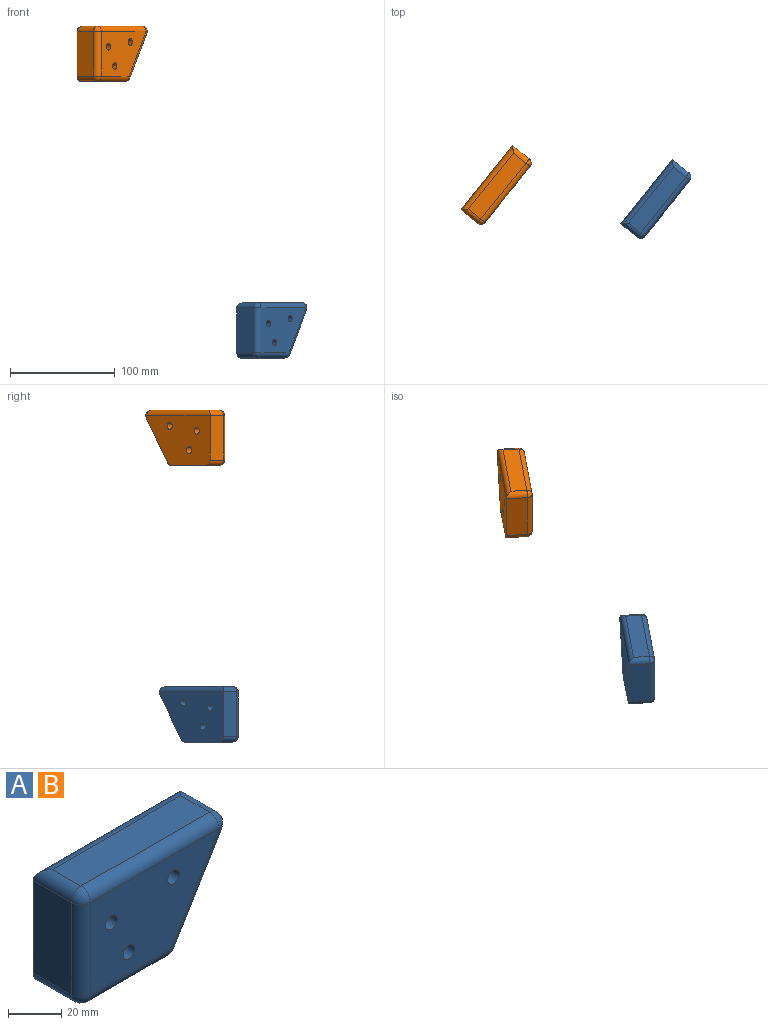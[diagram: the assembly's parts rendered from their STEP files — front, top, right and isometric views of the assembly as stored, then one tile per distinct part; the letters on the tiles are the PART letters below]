
ASSEMBLY  parts=2 mates=1
PART A: 22 faces, bbox 78.6x25.4x52.9 mm
  f0: plane 42.72x25.81mm, normal (0.86,0,-0.52), area 1014.3mm2, adj f5,f9,f11,f13
  f1: plane 68.47x15.24mm, normal (0,0,1), area 1043.5mm2, adj f6,f7,f8,f9
  f2: plane 42.72x20.32mm, normal (-1,0,0), area 868.1mm2, adj f5,f6,f10,f17
  f3: plane 42.66x20.32mm, normal (0,0,-1), area 866.8mm2, adj f5,f10,f11,f15
  f4: plane 68.47x42.72mm, normal (0,-1,0), area 2278.9mm2, adj f7,f13,f15,f17,f19,f20,f21
  f5: plane 78.63x47.8mm, normal (0,1,0), area 3006.8mm2, adj f0,f2,f3,f8,f9,f10,f11,f19
  f6: cylinder r=5.08mm len=20.32mm, axis (0,-1,0), area 147.4mm2, adj f1,f2,f8,f18
  f7: cylinder r=5.08mm len=68.47mm, axis (1,0,0), area 546.4mm2, adj f1,f4,f12,f18
  f8: cylinder r=5.08mm len=78.63mm, axis (-1,0,0), area 598mm2, adj f1,f5,f6,f9
  f9: cylinder r=5.08mm len=20.32mm, axis (0,-1,0), area 203.5mm2, adj f0,f1,f5,f8,f12
  f10: cylinder r=5.08mm len=20.32mm, axis (0,1,0), area 162.1mm2, adj f2,f3,f5,f16
  f11: cylinder r=5.08mm len=20.32mm, axis (0,1,0), area 106mm2, adj f0,f3,f5,f14
  f12: sphere r=5.08mm, area 54.6mm2, adj f7,f9,f13
  f13: cylinder r=5.08mm len=45.35mm, axis (-0.52,0,-0.86), area 398.3mm2, adj f0,f4,f12,f14
  f14: sphere r=5.08mm, area 26.5mm2, adj f11,f13,f15
  f15: cylinder r=5.08mm len=42.66mm, axis (-1,0,0), area 340.4mm2, adj f3,f4,f14,f16
  f16: sphere r=5.08mm, area 40.5mm2, adj f10,f15,f17
  f17: cylinder r=5.08mm len=42.72mm, axis (0,0,1), area 340.9mm2, adj f2,f4,f16,f18
  f18: sphere r=5.08mm, area 40.5mm2, adj f6,f7,f17
  f19: cylinder r=3.17mm len=25.4mm, axis (0,1,0), area 506.7mm2, adj f4,f5
  f20: cylinder r=3.17mm len=25.4mm, axis (0,1,0), area 506.7mm2, adj f4,f5
  f21: cylinder r=3.17mm len=25.4mm, axis (0,1,0), area 506.7mm2, adj f4,f5
PART B: same geometry as A
PLACE A rot(axis=(0,0,1),51.2deg) t=(223.58,74.11,-79.51)mm
PLACE B rot(axis=(0,0,1),51.2deg) t=(71.09,87.04,184.39)mm
MATE planar A.f20 <-> B.f20  axis (0.78,-0.63,0) through (222.6,32.32,-61.16)mm
